# Revit family: BIMLIB_Кран_шаровой_полнопроходной_РОСТерм
name_source: partatom
category: Арматура трубопроводов
revit_build: Autodesk Revit 2017 (Build: 20170118_1100(x64)
units: mm (PartAtom-declared; Revit-internal decimal feet)

## family parameters
Всегда вертикально = Да
На основе рабочей плоскости = Нет
Общий = Нет
При загрузке вырезать с полостями = Нет
Размер круглого соединителя = Использовать диаметр
Тип детали = Клапан - Вставляется

## types (1)
- BIMLIB_Кран_шаровой_полнопроходной_РОСТерм
    ADSK_URL документации изделия = http://rostherm.ru
    ADSK_URL страницы изделия = http://rostherm.ru
    ADSK_Версия Revit = 2017
    ADSK_Единица измерения = шт
    ADSK_Завод-изготовитель = РОСТерм
    ADSK_Материал = BIMLIB_Белый_РОСТерм
    BL_BIM library = https://bimlib.pro
    URL = http://rostherm.ru
    Изготовитель = РОСТерм
    Коэффициент K = 0.2
    Метод определения потерь = Коэффициент K
    Описание = Кран шаровой полнопроходной
    РТ_Материал_Гайка = BIMLIB_Черный_РОСТерм
